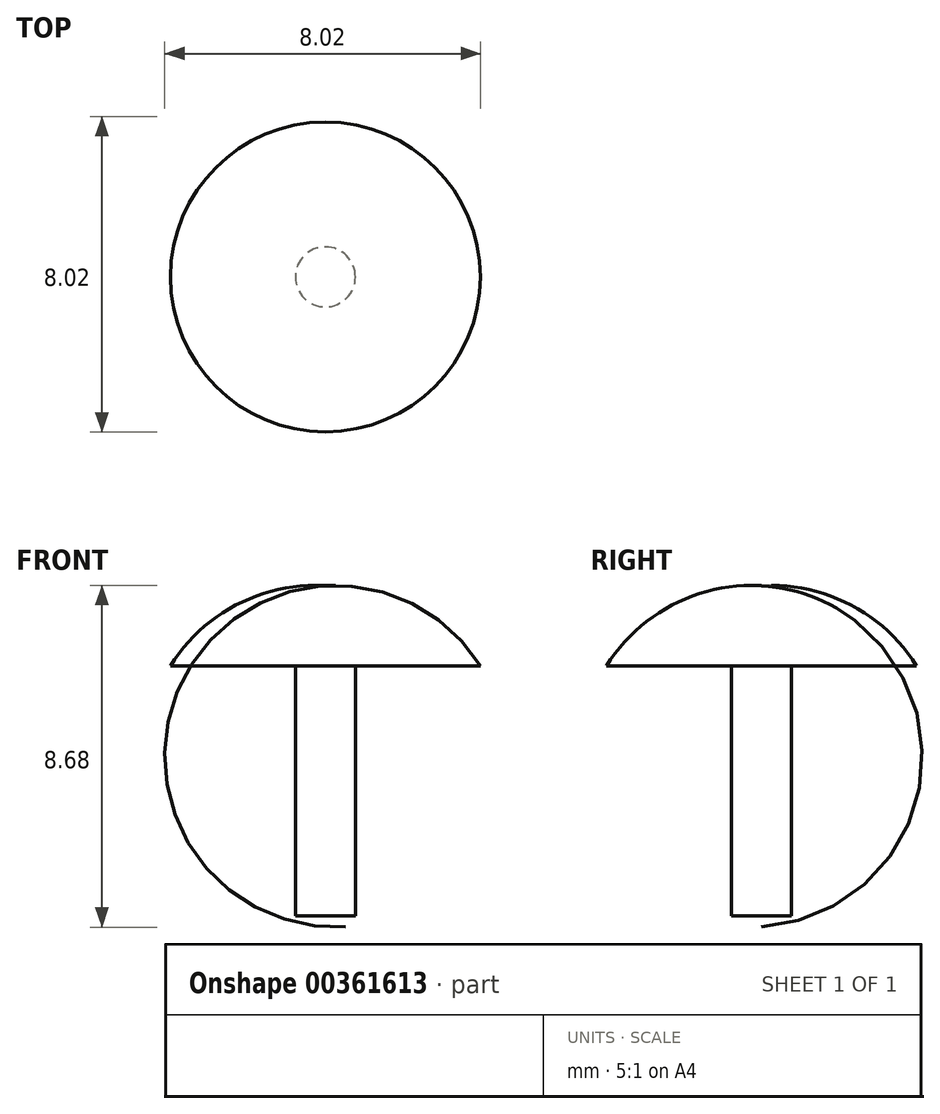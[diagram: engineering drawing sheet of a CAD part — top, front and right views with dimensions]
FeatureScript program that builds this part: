
annotation { "Feature Type Name" : "Feature", "Feature Type Description" : "" }
export const myFeature = defineFeature(function(context is Context, id is Id, definition is map)
    precondition{}
    {
        {
            var Q0;
            Q0=qCreatedBy(makeId("Front.planeOp"),FACE);
            var sketch = newSketch(context, id + "F0", { "sketchPlane" : qUnion([Q0])});
            skLineSegment(sketch, "E0", {"start": v(0, 3.15) * mm, "end": v(0, -3.85) * mm, "construction": true});
            skLineSegment(sketch, "E1", {"start": v(0, 0) * mm, "end": v(0.76, 0) * mm});
            skLineSegment(sketch, "E2", {"start": v(0.76, 0) * mm, "end": v(0.76, 6.35) * mm});
            skLineSegment(sketch, "E3", {"start": v(0, 6.35) * mm, "end": v(0, 0) * mm});
            skLineSegment(sketch, "E4", {"start": v(0, 6.35) * mm, "end": v(0.76, 6.35) * mm});
            skLineSegment(sketch, "E5", {"start": v(0.76, 6.35) * mm, "end": v(3.94, 6.35) * mm});
            skPoint(sketch, "E6", {"position": v(0, 8.38) * mm});
            skArc(sketch, "E7", {"start": v(3.94, 6.35) * mm, "mid": v(2.25, 7.9) * mm, "end": v(0, 8.38) * mm});
            skLineSegment(sketch, "E8", {"start": v(0, 8.38) * mm, "end": v(0, 6.35) * mm});
            skSolve(sketch);
        }
        {
            var Q0;
            Q0 = qSketchRegion(id + "F0", true);
            var Q1;
            Q1=sQuery(id+"F0.wireOp",EDGE,"E3");
            revolve(context, id + "F1", {"entities" : qUnion([Q0]), "axis" : qUnion([Q1]), "revolveType" : RevolveType.FULL});
        }
    });
